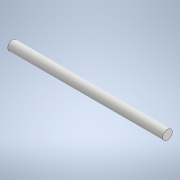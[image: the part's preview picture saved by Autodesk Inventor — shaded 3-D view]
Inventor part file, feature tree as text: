
AUTODESK INVENTOR PART (.ipt)
format: ipt  version: 2022 (Build 260153000, 153)  size: 94,720 bytes
history: native  units: mm
features: extrude x1, thread x1, sketch x1
ambient origin geometry x8: Origin, YZ Plane, XZ Plane, XY Plane, X Axis, Y Axis, Z Axis, Center Point
bodies: Solid1 (feature_tree)
feature tree (3):
  extrude  "Extrusion1"  Depth=130.0mm TaperAngle=0.0deg
  thread  "Thread1"  [1 undecoded]
  sketch  "Sketch1"  dims[d0=8.0mm d1=130.0mm d2=0.0mm d3=130.0mm d4=0.0mm]
note: 1 required parameter value undecoded (feature->parameter linkage not recoverable at this tier; creation-order binding heuristic only, values carry confidence <= 0.55)
